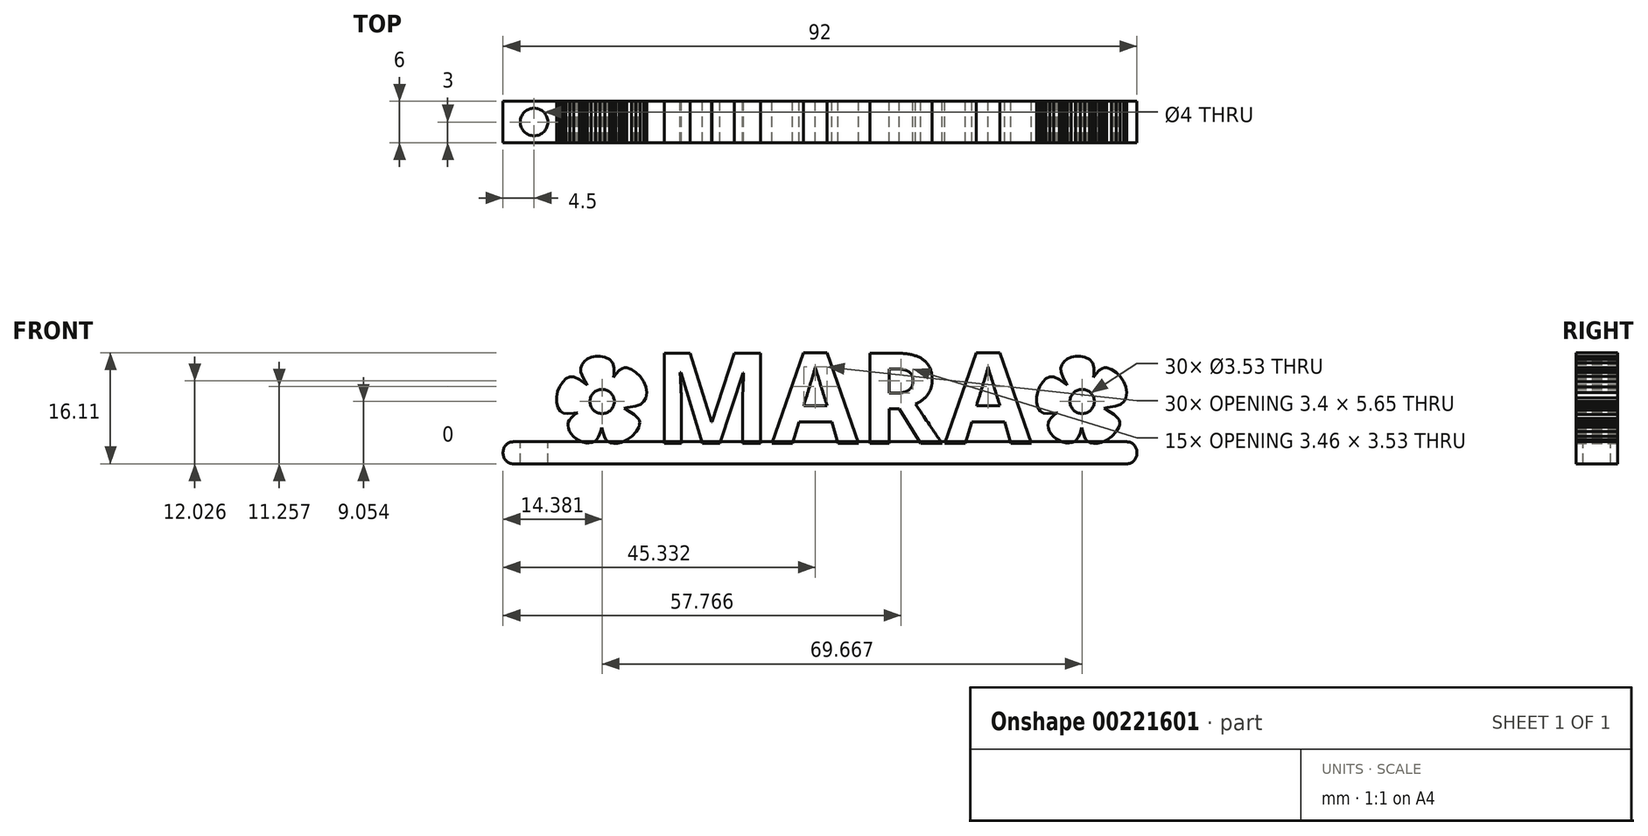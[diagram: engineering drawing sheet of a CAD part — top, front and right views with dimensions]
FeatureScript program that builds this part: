
annotation { "Feature Type Name" : "Feature", "Feature Type Description" : "" }
export const myFeature = defineFeature(function(context is Context, id is Id, definition is map)
    precondition{}
    {
        {
            var Q0;
            Q0=qCreatedBy(makeId("Front.planeOp"),FACE);
            var sketch = newSketch(context, id + "F0", { "sketchPlane" : qUnion([Q0])});
            skText(sketch, "E0", { "text": "   MARA", "fontName": "OpenSans-Bold.ttf"});
            skLineSegment(sketch, "E1.0.0", {"start": v(-9.3, 0.1) * mm, "end": v(-8.53, 0.46) * mm});
            skLineSegment(sketch, "E1.0.1", {"start": v(-8.53, 0.46) * mm, "end": v(-7.79, 1.02) * mm});
            skLineSegment(sketch, "E1.0.2", {"start": v(-7.79, 1.02) * mm, "end": v(-7.18, 1.67) * mm});
            skLineSegment(sketch, "E1.0.3", {"start": v(-7.18, 1.67) * mm, "end": v(-6.78, 2.35) * mm});
            skLineSegment(sketch, "E1.0.4", {"start": v(-6.78, 2.35) * mm, "end": v(-6.68, 2.7) * mm});
            skLineSegment(sketch, "E1.0.5", {"start": v(-6.68, 2.7) * mm, "end": v(-6.67, 3.02) * mm});
            skLineSegment(sketch, "E1.0.6", {"start": v(-6.67, 3.02) * mm, "end": v(-6.73, 3.33) * mm});
            skLineSegment(sketch, "E1.0.7", {"start": v(-6.73, 3.33) * mm, "end": v(-6.89, 3.62) * mm});
            skLineSegment(sketch, "E1.0.8", {"start": v(-6.89, 3.62) * mm, "end": v(-7.48, 4.2) * mm});
            skLineSegment(sketch, "E1.0.9", {"start": v(-7.48, 4.2) * mm, "end": v(-8.5, 4.79) * mm});
            skLineSegment(sketch, "E1.0.10", {"start": v(-8.5, 4.79) * mm, "end": v(-8.93, 5.06) * mm});
            skLineSegment(sketch, "E1.0.11", {"start": v(-8.93, 5.06) * mm, "end": v(-8.42, 5.16) * mm});
            skLineSegment(sketch, "E1.0.12", {"start": v(-8.42, 5.16) * mm, "end": v(-7.31, 5.37) * mm});
            skLineSegment(sketch, "E1.0.13", {"start": v(-7.31, 5.37) * mm, "end": v(-6.55, 5.65) * mm});
            skLineSegment(sketch, "E1.0.14", {"start": v(-6.55, 5.65) * mm, "end": v(-6.05, 6.04) * mm});
            skLineSegment(sketch, "E1.0.15", {"start": v(-6.05, 6.04) * mm, "end": v(-5.76, 6.58) * mm});
            skLineSegment(sketch, "E1.0.16", {"start": v(-5.76, 6.58) * mm, "end": v(-5.64, 7.33) * mm});
            skLineSegment(sketch, "E1.0.17", {"start": v(-5.64, 7.33) * mm, "end": v(-5.78, 8.14) * mm});
            skLineSegment(sketch, "E1.0.18", {"start": v(-5.78, 8.14) * mm, "end": v(-6.1, 8.93) * mm});
            skLineSegment(sketch, "E1.0.19", {"start": v(-6.1, 8.93) * mm, "end": v(-6.6, 9.67) * mm});
            skLineSegment(sketch, "E1.0.20", {"start": v(-6.6, 9.67) * mm, "end": v(-7.2, 10.28) * mm});
            skLineSegment(sketch, "E1.0.21", {"start": v(-7.2, 10.28) * mm, "end": v(-7.86, 10.72) * mm});
            skLineSegment(sketch, "E1.0.22", {"start": v(-7.86, 10.72) * mm, "end": v(-8.55, 10.93) * mm});
            skLineSegment(sketch, "E1.0.23", {"start": v(-8.55, 10.93) * mm, "end": v(-8.88, 10.93) * mm});
            skLineSegment(sketch, "E1.0.24", {"start": v(-8.88, 10.93) * mm, "end": v(-9.2, 10.85) * mm});
            skLineSegment(sketch, "E1.0.25", {"start": v(-9.2, 10.85) * mm, "end": v(-9.65, 10.56) * mm});
            skLineSegment(sketch, "E1.0.26", {"start": v(-9.65, 10.56) * mm, "end": v(-10.14, 9.98) * mm});
            skLineSegment(sketch, "E1.0.27", {"start": v(-10.14, 9.98) * mm, "end": v(-10.45, 9.58) * mm});
            skLineSegment(sketch, "E1.0.28", {"start": v(-10.45, 9.58) * mm, "end": v(-10.4, 10.03) * mm});
            skLineSegment(sketch, "E1.0.29", {"start": v(-10.4, 10.03) * mm, "end": v(-10.4, 10.93) * mm});
            skLineSegment(sketch, "E1.0.30", {"start": v(-10.4, 10.93) * mm, "end": v(-10.6, 11.63) * mm});
            skLineSegment(sketch, "E1.0.31", {"start": v(-10.6, 11.63) * mm, "end": v(-11.04, 12.15) * mm});
            skLineSegment(sketch, "E1.0.32", {"start": v(-11.04, 12.15) * mm, "end": v(-11.71, 12.5) * mm});
            skLineSegment(sketch, "E1.0.33", {"start": v(-11.71, 12.5) * mm, "end": v(-12.4, 12.64) * mm});
            skLineSegment(sketch, "E1.0.34", {"start": v(-12.4, 12.64) * mm, "end": v(-13.07, 12.62) * mm});
            skLineSegment(sketch, "E1.0.35", {"start": v(-13.07, 12.62) * mm, "end": v(-13.7, 12.47) * mm});
            skLineSegment(sketch, "E1.0.36", {"start": v(-13.7, 12.47) * mm, "end": v(-14.26, 12.2) * mm});
            skLineSegment(sketch, "E1.0.37", {"start": v(-14.26, 12.2) * mm, "end": v(-14.72, 11.83) * mm});
            skLineSegment(sketch, "E1.0.38", {"start": v(-14.72, 11.83) * mm, "end": v(-15.05, 11.38) * mm});
            skLineSegment(sketch, "E1.0.39", {"start": v(-15.05, 11.38) * mm, "end": v(-15.22, 10.87) * mm});
            skLineSegment(sketch, "E1.0.40", {"start": v(-15.22, 10.87) * mm, "end": v(-15.2, 10.3) * mm});
            skLineSegment(sketch, "E1.0.41", {"start": v(-15.2, 10.3) * mm, "end": v(-14.83, 9.4) * mm});
            skLineSegment(sketch, "E1.0.42", {"start": v(-14.83, 9.4) * mm, "end": v(-14.35, 8.55) * mm});
            skLineSegment(sketch, "E1.0.43", {"start": v(-14.35, 8.55) * mm, "end": v(-14.3, 8.4) * mm});
            skLineSegment(sketch, "E1.0.44", {"start": v(-14.3, 8.4) * mm, "end": v(-14.48, 8.53) * mm});
            skLineSegment(sketch, "E1.0.45", {"start": v(-14.48, 8.53) * mm, "end": v(-15.4, 9.23) * mm});
            skLineSegment(sketch, "E1.0.46", {"start": v(-15.4, 9.23) * mm, "end": v(-16.22, 9.63) * mm});
            skLineSegment(sketch, "E1.0.47", {"start": v(-16.22, 9.63) * mm, "end": v(-16.8, 9.63) * mm});
            skLineSegment(sketch, "E1.0.48", {"start": v(-16.8, 9.63) * mm, "end": v(-17.36, 9.37) * mm});
            skLineSegment(sketch, "E1.0.49", {"start": v(-17.36, 9.37) * mm, "end": v(-17.85, 8.9) * mm});
            skLineSegment(sketch, "E1.0.50", {"start": v(-17.85, 8.9) * mm, "end": v(-18.26, 8.26) * mm});
            skLineSegment(sketch, "E1.0.51", {"start": v(-18.26, 8.26) * mm, "end": v(-18.56, 7.51) * mm});
            skLineSegment(sketch, "E1.0.52", {"start": v(-18.56, 7.51) * mm, "end": v(-18.72, 6.71) * mm});
            skLineSegment(sketch, "E1.0.53", {"start": v(-18.72, 6.71) * mm, "end": v(-18.72, 5.9) * mm});
            skLineSegment(sketch, "E1.0.54", {"start": v(-18.72, 5.9) * mm, "end": v(-18.52, 5.16) * mm});
            skLineSegment(sketch, "E1.0.55", {"start": v(-18.52, 5.16) * mm, "end": v(-18.2, 4.64) * mm});
            skLineSegment(sketch, "E1.0.56", {"start": v(-18.2, 4.64) * mm, "end": v(-17.75, 4.36) * mm});
            skLineSegment(sketch, "E1.0.57", {"start": v(-17.75, 4.36) * mm, "end": v(-17.1, 4.27) * mm});
            skLineSegment(sketch, "E1.0.58", {"start": v(-17.1, 4.27) * mm, "end": v(-16.21, 4.37) * mm});
            skLineSegment(sketch, "E1.0.59", {"start": v(-16.21, 4.37) * mm, "end": v(-15.7, 4.43) * mm});
            skLineSegment(sketch, "E1.0.60", {"start": v(-15.7, 4.43) * mm, "end": v(-15.67, 4.4) * mm});
            skLineSegment(sketch, "E1.0.61", {"start": v(-15.67, 4.4) * mm, "end": v(-15.78, 4.33) * mm});
            skLineSegment(sketch, "E1.0.62", {"start": v(-15.78, 4.33) * mm, "end": v(-16.17, 4.07) * mm});
            skLineSegment(sketch, "E1.0.63", {"start": v(-16.17, 4.07) * mm, "end": v(-16.55, 3.71) * mm});
            skLineSegment(sketch, "E1.0.64", {"start": v(-16.55, 3.71) * mm, "end": v(-16.87, 3.33) * mm});
            skLineSegment(sketch, "E1.0.65", {"start": v(-16.87, 3.33) * mm, "end": v(-17.04, 3) * mm});
            skLineSegment(sketch, "E1.0.66", {"start": v(-17.04, 3) * mm, "end": v(-17.08, 2.6) * mm});
            skLineSegment(sketch, "E1.0.67", {"start": v(-17.08, 2.6) * mm, "end": v(-17.02, 2.2) * mm});
            skLineSegment(sketch, "E1.0.68", {"start": v(-17.02, 2.2) * mm, "end": v(-16.87, 1.78) * mm});
            skLineSegment(sketch, "E1.0.69", {"start": v(-16.87, 1.78) * mm, "end": v(-16.62, 1.39) * mm});
            skLineSegment(sketch, "E1.0.70", {"start": v(-16.62, 1.39) * mm, "end": v(-16.3, 1.02) * mm});
            skLineSegment(sketch, "E1.0.71", {"start": v(-16.3, 1.02) * mm, "end": v(-15.9, 0.69) * mm});
            skLineSegment(sketch, "E1.0.72", {"start": v(-15.9, 0.69) * mm, "end": v(-15.45, 0.4) * mm});
            skLineSegment(sketch, "E1.0.73", {"start": v(-15.45, 0.4) * mm, "end": v(-14.95, 0.2) * mm});
            skLineSegment(sketch, "E1.0.74", {"start": v(-14.95, 0.2) * mm, "end": v(-14.44, 0.06) * mm});
            skLineSegment(sketch, "E1.0.75", {"start": v(-14.44, 0.06) * mm, "end": v(-13.98, 0.02) * mm});
            skLineSegment(sketch, "E1.0.76", {"start": v(-13.98, 0.02) * mm, "end": v(-13.58, 0.08) * mm});
            skLineSegment(sketch, "E1.0.77", {"start": v(-13.58, 0.08) * mm, "end": v(-13.23, 0.23) * mm});
            skLineSegment(sketch, "E1.0.78", {"start": v(-13.23, 0.23) * mm, "end": v(-12.92, 0.49) * mm});
            skLineSegment(sketch, "E1.0.79", {"start": v(-12.92, 0.49) * mm, "end": v(-12.67, 0.84) * mm});
            skLineSegment(sketch, "E1.0.80", {"start": v(-12.67, 0.84) * mm, "end": v(-12.46, 1.28) * mm});
            skLineSegment(sketch, "E1.0.81", {"start": v(-12.46, 1.28) * mm, "end": v(-12.3, 1.83) * mm});
            skLineSegment(sketch, "E1.0.82", {"start": v(-12.3, 1.83) * mm, "end": v(-12.19, 2.26) * mm});
            skLineSegment(sketch, "E1.0.83", {"start": v(-12.19, 2.26) * mm, "end": v(-12.13, 2.1) * mm});
            skLineSegment(sketch, "E1.0.84", {"start": v(-12.13, 2.1) * mm, "end": v(-12.01, 1.53) * mm});
            skLineSegment(sketch, "E1.0.85", {"start": v(-12.01, 1.53) * mm, "end": v(-11.82, 1) * mm});
            skLineSegment(sketch, "E1.0.86", {"start": v(-11.82, 1) * mm, "end": v(-11.6, 0.55) * mm});
            skLineSegment(sketch, "E1.0.87", {"start": v(-11.6, 0.55) * mm, "end": v(-11.35, 0.26) * mm});
            skLineSegment(sketch, "E1.0.88", {"start": v(-11.35, 0.26) * mm, "end": v(-10.95, 0.05) * mm});
            skLineSegment(sketch, "E1.0.89", {"start": v(-10.95, 0.05) * mm, "end": v(-10.46, -0.04) * mm});
            skLineSegment(sketch, "E1.0.90", {"start": v(-10.46, -0.04) * mm, "end": v(-9.9, -0.03) * mm});
            skLineSegment(sketch, "E1.0.91", {"start": v(-9.9, -0.03) * mm, "end": v(-9.3, 0.1) * mm});
            skCircle(sketch, "E2", {"center": v(-12.12, 6.05) * mm, "radius": 1.77 * mm});
            skCircle(sketch, "E3.1.0.0", {"center": v(57.55, 6.05) * mm, "radius": 1.77 * mm});
            skLineSegment(sketch, "E3.1.0.1", {"start": v(59.22, 9.58) * mm, "end": v(59.26, 10.03) * mm});
            skLineSegment(sketch, "E3.1.0.2", {"start": v(62.47, 10.28) * mm, "end": v(61.8, 10.72) * mm});
            skLineSegment(sketch, "E3.1.0.3", {"start": v(50.95, 5.9) * mm, "end": v(51.15, 5.16) * mm});
            skLineSegment(sketch, "E3.1.0.4", {"start": v(55.4, 12.2) * mm, "end": v(54.94, 11.83) * mm});
            skLineSegment(sketch, "E3.1.0.5", {"start": v(53.37, 1.02) * mm, "end": v(53.76, 0.69) * mm});
            skLineSegment(sketch, "E3.1.0.6", {"start": v(53.45, 9.63) * mm, "end": v(52.86, 9.63) * mm});
            skLineSegment(sketch, "E3.1.0.7", {"start": v(51.1, 7.51) * mm, "end": v(50.95, 6.71) * mm});
            skLineSegment(sketch, "E3.1.0.8", {"start": v(54.27, 9.23) * mm, "end": v(53.45, 9.63) * mm});
            skLineSegment(sketch, "E3.1.0.9", {"start": v(52.86, 9.63) * mm, "end": v(52.31, 9.37) * mm});
            skLineSegment(sketch, "E3.1.0.10", {"start": v(59.53, 9.98) * mm, "end": v(59.22, 9.58) * mm});
            skLineSegment(sketch, "E3.1.0.11", {"start": v(59.07, 11.63) * mm, "end": v(58.63, 12.15) * mm});
            skLineSegment(sketch, "E3.1.0.12", {"start": v(58.63, 12.15) * mm, "end": v(57.95, 12.5) * mm});
            skLineSegment(sketch, "E3.1.0.13", {"start": v(59.28, 10.93) * mm, "end": v(59.07, 11.63) * mm});
            skLineSegment(sketch, "E3.1.0.14", {"start": v(54.21, 0.4) * mm, "end": v(54.72, 0.2) * mm});
            skLineSegment(sketch, "E3.1.0.15", {"start": v(59.77, -0.03) * mm, "end": v(60.36, 0.1) * mm});
            skLineSegment(sketch, "E3.1.0.16", {"start": v(50.95, 6.71) * mm, "end": v(50.95, 5.9) * mm});
            skLineSegment(sketch, "E3.1.0.17", {"start": v(60.36, 0.1) * mm, "end": v(61.14, 0.46) * mm});
            skLineSegment(sketch, "E3.1.0.18", {"start": v(53.76, 0.69) * mm, "end": v(54.21, 0.4) * mm});
            skLineSegment(sketch, "E3.1.0.19", {"start": v(51.15, 5.16) * mm, "end": v(51.47, 4.64) * mm});
            skLineSegment(sketch, "E3.1.0.20", {"start": v(62.35, 5.37) * mm, "end": v(63.12, 5.65) * mm});
            skLineSegment(sketch, "E3.1.0.21", {"start": v(61.14, 0.46) * mm, "end": v(61.88, 1.02) * mm});
            skLineSegment(sketch, "E3.1.0.22", {"start": v(63.07, 9.67) * mm, "end": v(62.47, 10.28) * mm});
            skLineSegment(sketch, "E3.1.0.23", {"start": v(59.26, 10.03) * mm, "end": v(59.28, 10.93) * mm});
            skLineSegment(sketch, "E3.1.0.24", {"start": v(52.31, 9.37) * mm, "end": v(51.81, 8.9) * mm});
            skLineSegment(sketch, "E3.1.0.25", {"start": v(57.95, 12.5) * mm, "end": v(57.27, 12.64) * mm});
            skLineSegment(sketch, "E3.1.0.26", {"start": v(56.6, 12.62) * mm, "end": v(55.96, 12.47) * mm});
            skLineSegment(sketch, "E3.1.0.27", {"start": v(62.5, 1.67) * mm, "end": v(62.88, 2.35) * mm});
            skLineSegment(sketch, "E3.1.0.28", {"start": v(63.56, 8.93) * mm, "end": v(63.07, 9.67) * mm});
            skLineSegment(sketch, "E3.1.0.29", {"start": v(57.27, 12.64) * mm, "end": v(56.6, 12.62) * mm});
            skLineSegment(sketch, "E3.1.0.30", {"start": v(61.88, 1.02) * mm, "end": v(62.5, 1.67) * mm});
            skLineSegment(sketch, "E3.1.0.31", {"start": v(51.81, 8.9) * mm, "end": v(51.4, 8.26) * mm});
            skLineSegment(sketch, "E3.1.0.32", {"start": v(51.4, 8.26) * mm, "end": v(51.1, 7.51) * mm});
            skLineSegment(sketch, "E3.1.0.33", {"start": v(55.96, 12.47) * mm, "end": v(55.4, 12.2) * mm});
            skLineSegment(sketch, "E3.1.0.34", {"start": v(62.88, 2.35) * mm, "end": v(62.98, 2.7) * mm});
            skLineSegment(sketch, "E3.1.0.35", {"start": v(52.86, 9.63) * mm, "end": v(52.31, 9.37) * mm});
            skLineSegment(sketch, "E3.1.0.36", {"start": v(57.27, 12.64) * mm, "end": v(56.6, 12.62) * mm});
            skLineSegment(sketch, "E3.1.0.37", {"start": v(62.35, 5.37) * mm, "end": v(63.12, 5.65) * mm});
            skLineSegment(sketch, "E3.1.0.38", {"start": v(58.71, 0.05) * mm, "end": v(59.21, -0.04) * mm});
            skLineSegment(sketch, "E3.1.0.39", {"start": v(63.56, 8.93) * mm, "end": v(63.07, 9.67) * mm});
            skLineSegment(sketch, "E3.1.0.40", {"start": v(59.77, -0.03) * mm, "end": v(60.36, 0.1) * mm});
            skLineSegment(sketch, "E3.1.0.41", {"start": v(59.53, 9.98) * mm, "end": v(59.22, 9.58) * mm});
            skLineSegment(sketch, "E3.1.0.42", {"start": v(61.88, 1.02) * mm, "end": v(62.5, 1.67) * mm});
            skLineSegment(sketch, "E3.1.0.43", {"start": v(62.88, 2.35) * mm, "end": v(62.98, 2.7) * mm});
            skLineSegment(sketch, "E3.1.0.44", {"start": v(50.95, 6.71) * mm, "end": v(50.95, 5.9) * mm});
            skLineSegment(sketch, "E3.1.0.45", {"start": v(60.36, 0.1) * mm, "end": v(61.14, 0.46) * mm});
            skLineSegment(sketch, "E3.1.0.46", {"start": v(56.6, 12.62) * mm, "end": v(55.96, 12.47) * mm});
            skLineSegment(sketch, "E3.1.0.47", {"start": v(55.4, 12.2) * mm, "end": v(54.94, 11.83) * mm});
            skLineSegment(sketch, "E3.1.0.48", {"start": v(54.21, 0.4) * mm, "end": v(54.72, 0.2) * mm});
            skLineSegment(sketch, "E3.1.0.49", {"start": v(59.26, 10.03) * mm, "end": v(59.28, 10.93) * mm});
            skLineSegment(sketch, "E3.1.0.50", {"start": v(59.22, 9.58) * mm, "end": v(59.26, 10.03) * mm});
            skLineSegment(sketch, "E3.1.0.51", {"start": v(59.21, -0.04) * mm, "end": v(59.77, -0.03) * mm});
            skLineSegment(sketch, "E3.1.0.52", {"start": v(53.45, 9.63) * mm, "end": v(52.86, 9.63) * mm});
            skLineSegment(sketch, "E3.1.0.53", {"start": v(59.28, 10.93) * mm, "end": v(59.07, 11.63) * mm});
            skLineSegment(sketch, "E3.1.0.54", {"start": v(62.47, 10.28) * mm, "end": v(61.8, 10.72) * mm});
            skLineSegment(sketch, "E3.1.0.55", {"start": v(51.81, 8.9) * mm, "end": v(51.4, 8.26) * mm});
            skLineSegment(sketch, "E3.1.0.56", {"start": v(53.76, 0.69) * mm, "end": v(54.21, 0.4) * mm});
            skLineSegment(sketch, "E3.1.0.57", {"start": v(57.95, 12.5) * mm, "end": v(57.27, 12.64) * mm});
            skLineSegment(sketch, "E3.1.0.58", {"start": v(52.31, 9.37) * mm, "end": v(51.81, 8.9) * mm});
            skLineSegment(sketch, "E3.1.0.59", {"start": v(50.95, 5.9) * mm, "end": v(51.15, 5.16) * mm});
            skLineSegment(sketch, "E3.1.0.60", {"start": v(58.63, 12.15) * mm, "end": v(57.95, 12.5) * mm});
            skLineSegment(sketch, "E3.1.0.61", {"start": v(54.27, 9.23) * mm, "end": v(53.45, 9.63) * mm});
            skLineSegment(sketch, "E3.1.0.62", {"start": v(61.14, 0.46) * mm, "end": v(61.88, 1.02) * mm});
            skLineSegment(sketch, "E3.1.0.63", {"start": v(59.07, 11.63) * mm, "end": v(58.63, 12.15) * mm});
            skLineSegment(sketch, "E3.1.0.64", {"start": v(51.4, 8.26) * mm, "end": v(51.1, 7.51) * mm});
            skLineSegment(sketch, "E3.1.0.65", {"start": v(62.5, 1.67) * mm, "end": v(62.88, 2.35) * mm});
            skLineSegment(sketch, "E3.1.0.66", {"start": v(51.1, 7.51) * mm, "end": v(50.95, 6.71) * mm});
            skLineSegment(sketch, "E3.1.0.67", {"start": v(53.37, 1.02) * mm, "end": v(53.76, 0.69) * mm});
            skLineSegment(sketch, "E3.1.0.68", {"start": v(51.15, 5.16) * mm, "end": v(51.47, 4.64) * mm});
            skLineSegment(sketch, "E3.1.0.69", {"start": v(55.96, 12.47) * mm, "end": v(55.4, 12.2) * mm});
            skLineSegment(sketch, "E3.1.0.70", {"start": v(63.07, 9.67) * mm, "end": v(62.47, 10.28) * mm});
            skLineSegment(sketch, "E3.1.0.71", {"start": v(54.94, 11.83) * mm, "end": v(54.61, 11.38) * mm});
            skLineSegment(sketch, "E3.1.0.72", {"start": v(61.8, 10.72) * mm, "end": v(61.12, 10.93) * mm});
            skLineSegment(sketch, "E3.1.0.73", {"start": v(63.61, 6.04) * mm, "end": v(63.91, 6.58) * mm});
            skLineSegment(sketch, "E3.1.0.74", {"start": v(62.98, 2.7) * mm, "end": v(63, 3.02) * mm});
            skLineSegment(sketch, "E3.1.0.75", {"start": v(61.12, 10.93) * mm, "end": v(60.79, 10.93) * mm});
            skLineSegment(sketch, "E3.1.0.76", {"start": v(51.47, 4.64) * mm, "end": v(51.92, 4.36) * mm});
            skLineSegment(sketch, "E3.1.0.77", {"start": v(60.46, 10.85) * mm, "end": v(60.02, 10.56) * mm});
            skLineSegment(sketch, "E3.1.0.78", {"start": v(61.25, 5.16) * mm, "end": v(62.35, 5.37) * mm});
            skLineSegment(sketch, "E3.1.0.79", {"start": v(63, 3.02) * mm, "end": v(62.94, 3.33) * mm});
            skLineSegment(sketch, "E3.1.0.80", {"start": v(62.94, 3.33) * mm, "end": v(62.78, 3.62) * mm});
            skLineSegment(sketch, "E3.1.0.81", {"start": v(62.18, 4.2) * mm, "end": v(61.17, 4.79) * mm});
            skLineSegment(sketch, "E3.1.0.82", {"start": v(64.02, 7.33) * mm, "end": v(63.9, 8.14) * mm});
            skLineSegment(sketch, "E3.1.0.83", {"start": v(53.04, 1.39) * mm, "end": v(53.37, 1.02) * mm});
            skLineSegment(sketch, "E3.1.0.84", {"start": v(55.23, 0.06) * mm, "end": v(55.68, 0.02) * mm});
            skLineSegment(sketch, "E3.1.0.85", {"start": v(60.74, 5.06) * mm, "end": v(61.25, 5.16) * mm});
            skLineSegment(sketch, "E3.1.0.86", {"start": v(58.31, 0.26) * mm, "end": v(58.71, 0.05) * mm});
            skLineSegment(sketch, "E3.1.0.87", {"start": v(54.61, 11.38) * mm, "end": v(54.45, 10.87) * mm});
            skLineSegment(sketch, "E3.1.0.88", {"start": v(63.91, 6.58) * mm, "end": v(64.02, 7.33) * mm});
            skLineSegment(sketch, "E3.1.0.89", {"start": v(58.71, 0.05) * mm, "end": v(59.21, -0.04) * mm});
            skLineSegment(sketch, "E3.1.0.90", {"start": v(61.17, 4.79) * mm, "end": v(60.74, 5.06) * mm});
            skLineSegment(sketch, "E3.1.0.91", {"start": v(54.72, 0.2) * mm, "end": v(55.23, 0.06) * mm});
            skLineSegment(sketch, "E3.1.0.92", {"start": v(54.47, 10.3) * mm, "end": v(54.84, 9.4) * mm});
            skLineSegment(sketch, "E3.1.0.93", {"start": v(52.8, 1.78) * mm, "end": v(53.04, 1.39) * mm});
            skLineSegment(sketch, "E3.1.0.94", {"start": v(62.78, 3.62) * mm, "end": v(62.18, 4.2) * mm});
            skLineSegment(sketch, "E3.1.0.95", {"start": v(59.21, -0.04) * mm, "end": v(59.77, -0.03) * mm});
            skLineSegment(sketch, "E3.1.0.96", {"start": v(54.45, 10.87) * mm, "end": v(54.47, 10.3) * mm});
            skLineSegment(sketch, "E3.1.0.97", {"start": v(63.12, 5.65) * mm, "end": v(63.61, 6.04) * mm});
            skLineSegment(sketch, "E3.1.0.98", {"start": v(60.79, 10.93) * mm, "end": v(60.46, 10.85) * mm});
            skLineSegment(sketch, "E3.1.0.99", {"start": v(60.02, 10.56) * mm, "end": v(59.53, 9.98) * mm});
            skLineSegment(sketch, "E3.1.0.100", {"start": v(55.68, 0.02) * mm, "end": v(56.09, 0.08) * mm});
            skLineSegment(sketch, "E3.1.0.101", {"start": v(52.64, 2.2) * mm, "end": v(52.8, 1.78) * mm});
            skLineSegment(sketch, "E3.1.0.102", {"start": v(63.9, 8.14) * mm, "end": v(63.56, 8.93) * mm});
            skLineSegment(sketch, "E3.1.0.103", {"start": v(61.17, 4.79) * mm, "end": v(60.74, 5.06) * mm});
            skLineSegment(sketch, "E3.1.0.104", {"start": v(60.74, 5.06) * mm, "end": v(61.25, 5.16) * mm});
            skLineSegment(sketch, "E3.1.0.105", {"start": v(51.47, 4.64) * mm, "end": v(51.92, 4.36) * mm});
            skLineSegment(sketch, "E3.1.0.106", {"start": v(58.07, 0.55) * mm, "end": v(58.31, 0.26) * mm});
            skLineSegment(sketch, "E3.1.0.107", {"start": v(58.31, 0.26) * mm, "end": v(58.71, 0.05) * mm});
            skLineSegment(sketch, "E3.1.0.108", {"start": v(52.8, 1.78) * mm, "end": v(53.04, 1.39) * mm});
            skLineSegment(sketch, "E3.1.0.109", {"start": v(62.78, 3.62) * mm, "end": v(62.18, 4.2) * mm});
            skLineSegment(sketch, "E3.1.0.110", {"start": v(61.25, 5.16) * mm, "end": v(62.35, 5.37) * mm});
            skLineSegment(sketch, "E3.1.0.111", {"start": v(54.47, 10.3) * mm, "end": v(54.84, 9.4) * mm});
            skLineSegment(sketch, "E3.1.0.112", {"start": v(63.12, 5.65) * mm, "end": v(63.61, 6.04) * mm});
            skLineSegment(sketch, "E3.1.0.113", {"start": v(60.02, 10.56) * mm, "end": v(59.53, 9.98) * mm});
            skLineSegment(sketch, "E3.1.0.114", {"start": v(63.91, 6.58) * mm, "end": v(64.02, 7.33) * mm});
            skLineSegment(sketch, "E3.1.0.115", {"start": v(54.45, 10.87) * mm, "end": v(54.47, 10.3) * mm});
            skLineSegment(sketch, "E3.1.0.116", {"start": v(60.79, 10.93) * mm, "end": v(60.46, 10.85) * mm});
            skLineSegment(sketch, "E3.1.0.117", {"start": v(55.68, 0.02) * mm, "end": v(56.09, 0.08) * mm});
            skLineSegment(sketch, "E3.1.0.118", {"start": v(60.46, 10.85) * mm, "end": v(60.02, 10.56) * mm});
            skLineSegment(sketch, "E3.1.0.119", {"start": v(55.23, 0.06) * mm, "end": v(55.68, 0.02) * mm});
            skLineSegment(sketch, "E3.1.0.120", {"start": v(54.72, 0.2) * mm, "end": v(55.23, 0.06) * mm});
            skLineSegment(sketch, "E3.1.0.121", {"start": v(62.18, 4.2) * mm, "end": v(61.17, 4.79) * mm});
            skLineSegment(sketch, "E3.1.0.122", {"start": v(63.61, 6.04) * mm, "end": v(63.91, 6.58) * mm});
            skLineSegment(sketch, "E3.1.0.123", {"start": v(52.58, 2.6) * mm, "end": v(52.64, 2.2) * mm});
            skLineSegment(sketch, "E3.1.0.124", {"start": v(62.98, 2.7) * mm, "end": v(63, 3.02) * mm});
            skLineSegment(sketch, "E3.1.0.125", {"start": v(53.04, 1.39) * mm, "end": v(53.37, 1.02) * mm});
            skLineSegment(sketch, "E3.1.0.126", {"start": v(63.9, 8.14) * mm, "end": v(63.56, 8.93) * mm});
            skLineSegment(sketch, "E3.1.0.127", {"start": v(64.02, 7.33) * mm, "end": v(63.9, 8.14) * mm});
            skLineSegment(sketch, "E3.1.0.128", {"start": v(63, 3.02) * mm, "end": v(62.94, 3.33) * mm});
            skLineSegment(sketch, "E3.1.0.129", {"start": v(52.64, 2.2) * mm, "end": v(52.8, 1.78) * mm});
            skLineSegment(sketch, "E3.1.0.130", {"start": v(62.94, 3.33) * mm, "end": v(62.78, 3.62) * mm});
            skLineSegment(sketch, "E3.1.0.131", {"start": v(54.61, 11.38) * mm, "end": v(54.45, 10.87) * mm});
            skLineSegment(sketch, "E3.1.0.132", {"start": v(61.12, 10.93) * mm, "end": v(60.79, 10.93) * mm});
            skLineSegment(sketch, "E3.1.0.133", {"start": v(61.8, 10.72) * mm, "end": v(61.12, 10.93) * mm});
            skLineSegment(sketch, "E3.1.0.134", {"start": v(54.94, 11.83) * mm, "end": v(54.61, 11.38) * mm});
            skLineSegment(sketch, "E3.1.0.135", {"start": v(52.58, 2.6) * mm, "end": v(52.64, 2.2) * mm});
            skLineSegment(sketch, "E3.1.0.136", {"start": v(53.45, 4.37) * mm, "end": v(53.96, 4.43) * mm});
            skLineSegment(sketch, "E3.1.0.137", {"start": v(57.66, 1.53) * mm, "end": v(57.84, 1) * mm});
            skLineSegment(sketch, "E3.1.0.138", {"start": v(53.89, 4.33) * mm, "end": v(53.5, 4.07) * mm});
            skLineSegment(sketch, "E3.1.0.139", {"start": v(56.44, 0.23) * mm, "end": v(56.74, 0.49) * mm});
            skLineSegment(sketch, "E3.1.0.140", {"start": v(57, 0.84) * mm, "end": v(57.2, 1.28) * mm});
            skLineSegment(sketch, "E3.1.0.141", {"start": v(57.84, 1) * mm, "end": v(58.07, 0.55) * mm});
            skLineSegment(sketch, "E3.1.0.142", {"start": v(53.5, 4.07) * mm, "end": v(53.11, 3.71) * mm});
            skLineSegment(sketch, "E3.1.0.143", {"start": v(57.54, 2.1) * mm, "end": v(57.66, 1.53) * mm});
            skLineSegment(sketch, "E3.1.0.144", {"start": v(56.74, 0.49) * mm, "end": v(57, 0.84) * mm});
            skLineSegment(sketch, "E3.1.0.145", {"start": v(52.56, 4.27) * mm, "end": v(53.45, 4.37) * mm});
            skLineSegment(sketch, "E3.1.0.146", {"start": v(53.11, 3.71) * mm, "end": v(52.8, 3.33) * mm});
            skLineSegment(sketch, "E3.1.0.147", {"start": v(51.92, 4.36) * mm, "end": v(52.56, 4.27) * mm});
            skLineSegment(sketch, "E3.1.0.148", {"start": v(57.2, 1.28) * mm, "end": v(57.36, 1.83) * mm});
            skLineSegment(sketch, "E3.1.0.149", {"start": v(57.48, 2.26) * mm, "end": v(57.54, 2.1) * mm});
            skLineSegment(sketch, "E3.1.0.150", {"start": v(52.8, 3.33) * mm, "end": v(52.63, 3) * mm});
            skLineSegment(sketch, "E3.1.0.151", {"start": v(58.07, 0.55) * mm, "end": v(58.31, 0.26) * mm});
            skLineSegment(sketch, "E3.1.0.152", {"start": v(57.36, 1.83) * mm, "end": v(57.48, 2.26) * mm});
            skLineSegment(sketch, "E3.1.0.153", {"start": v(52.63, 3) * mm, "end": v(52.58, 2.6) * mm});
            skLineSegment(sketch, "E3.1.0.154", {"start": v(56.09, 0.08) * mm, "end": v(56.44, 0.23) * mm});
            skLineSegment(sketch, "E3.1.0.155", {"start": v(54, 4.4) * mm, "end": v(53.89, 4.33) * mm});
            skLineSegment(sketch, "E3.1.0.156", {"start": v(57.48, 2.26) * mm, "end": v(57.54, 2.1) * mm});
            skLineSegment(sketch, "E3.1.0.157", {"start": v(52.56, 4.27) * mm, "end": v(53.45, 4.37) * mm});
            skLineSegment(sketch, "E3.1.0.158", {"start": v(57.66, 1.53) * mm, "end": v(57.84, 1) * mm});
            skLineSegment(sketch, "E3.1.0.159", {"start": v(53.96, 4.43) * mm, "end": v(54, 4.4) * mm});
            skLineSegment(sketch, "E3.1.0.160", {"start": v(53.11, 3.71) * mm, "end": v(52.8, 3.33) * mm});
            skLineSegment(sketch, "E3.1.0.161", {"start": v(51.92, 4.36) * mm, "end": v(52.56, 4.27) * mm});
            skLineSegment(sketch, "E3.1.0.162", {"start": v(53.45, 4.37) * mm, "end": v(53.96, 4.43) * mm});
            skLineSegment(sketch, "E3.1.0.163", {"start": v(56.09, 0.08) * mm, "end": v(56.44, 0.23) * mm});
            skLineSegment(sketch, "E3.1.0.164", {"start": v(53.5, 4.07) * mm, "end": v(53.11, 3.71) * mm});
            skLineSegment(sketch, "E3.1.0.165", {"start": v(57.54, 2.1) * mm, "end": v(57.66, 1.53) * mm});
            skLineSegment(sketch, "E3.1.0.166", {"start": v(57.36, 1.83) * mm, "end": v(57.48, 2.26) * mm});
            skLineSegment(sketch, "E3.1.0.167", {"start": v(53.89, 4.33) * mm, "end": v(53.5, 4.07) * mm});
            skLineSegment(sketch, "E3.1.0.168", {"start": v(56.44, 0.23) * mm, "end": v(56.74, 0.49) * mm});
            skLineSegment(sketch, "E3.1.0.169", {"start": v(52.63, 3) * mm, "end": v(52.58, 2.6) * mm});
            skLineSegment(sketch, "E3.1.0.170", {"start": v(57.84, 1) * mm, "end": v(58.07, 0.55) * mm});
            skLineSegment(sketch, "E3.1.0.171", {"start": v(56.74, 0.49) * mm, "end": v(57, 0.84) * mm});
            skLineSegment(sketch, "E3.1.0.172", {"start": v(57, 0.84) * mm, "end": v(57.2, 1.28) * mm});
            skLineSegment(sketch, "E3.1.0.173", {"start": v(52.8, 3.33) * mm, "end": v(52.63, 3) * mm});
            skLineSegment(sketch, "E3.1.0.174", {"start": v(57.2, 1.28) * mm, "end": v(57.36, 1.83) * mm});
            skLineSegment(sketch, "E3.1.0.175", {"start": v(54, 4.4) * mm, "end": v(53.89, 4.33) * mm});
            skLineSegment(sketch, "E3.1.0.176", {"start": v(53.96, 4.43) * mm, "end": v(54, 4.4) * mm});
            skLineSegment(sketch, "E3.1.0.177", {"start": v(55.38, 8.4) * mm, "end": v(55.19, 8.53) * mm});
            skLineSegment(sketch, "E3.1.0.178", {"start": v(55.31, 8.55) * mm, "end": v(55.38, 8.4) * mm});
            skLineSegment(sketch, "E3.1.0.179", {"start": v(54.84, 9.4) * mm, "end": v(55.31, 8.55) * mm});
            skLineSegment(sketch, "E3.1.0.180", {"start": v(55.19, 8.53) * mm, "end": v(54.27, 9.23) * mm});
            skLineSegment(sketch, "E3.1.0.181", {"start": v(55.31, 8.55) * mm, "end": v(55.38, 8.4) * mm});
            skLineSegment(sketch, "E3.1.0.182", {"start": v(54.84, 9.4) * mm, "end": v(55.31, 8.55) * mm});
            skLineSegment(sketch, "E3.1.0.183", {"start": v(55.19, 8.53) * mm, "end": v(54.27, 9.23) * mm});
            skLineSegment(sketch, "E3.1.0.184", {"start": v(55.38, 8.4) * mm, "end": v(55.19, 8.53) * mm});
            skLineSegment(sketch, "E3.direction1", {"start": v(-16.3, 1.02) * mm, "end": v(42.4, 1.02) * mm, "construction": true});
            const initialGuessF0  = {"E0": [-0.019, 0, 1, 0, 0.01317]};
            skSetInitialGuess(sketch, initialGuessF0);
            skSolve(sketch);
        }
        {
            var Q0;
            Q0=qSketchRegion(id+"F0",true);
            extrude(context, id + "F1", {"entities" : qUnion([Q0]), "endBound" : BoundingType.SYMMETRIC, "depth" : 6 * mm});
        }
        {
            var Q0;
            Q0=qCreatedBy(makeId("Top.planeOp"),FACE);
            var sketch = newSketch(context, id + "F2", { "sketchPlane" : qUnion([Q0])});
            skLineSegment(sketch, "E4.bottom", {"start": v(-19, 3) * mm, "end": v(65.5, 3) * mm});
            skLineSegment(sketch, "E4.top", {"start": v(-19, -3) * mm, "end": v(65.5, -3) * mm});
            skLineSegment(sketch, "E4.left", {"start": v(-19, 3) * mm, "end": v(-19, -3) * mm});
            skLineSegment(sketch, "E4.right", {"start": v(65.5, 3) * mm, "end": v(65.5, -3) * mm});
            skSolve(sketch);
        }
        {
            var Q0;
            Q0=makeQuery(id+"F2.imprint","IMPRINT",FACE,{"disambiguationData":[TD([[makeQuery(id+"F2.imprint","IMPRINT",EDGE,{"derivedFrom":sQuery(id+"F2.wireOp",EDGE,"E4.bottom")}),-1.0]])]});
            extrude(context, id + "F3", {"entities" : qUnion([Q0]), "depth" : 0.2 * mm});
        }
        {
            var Q0;
            Q0=makeQuery(id+"F3.opExtrude","CAP_FACE",FACE,{"disambiguationData":[OSD([sQuery(id+"F2.wireOp",EDGE,"E4.bottom"),sQuery(id+"F2.wireOp",EDGE,"E4.top"),sQuery(id+"F2.wireOp",EDGE,"E4.left"),sQuery(id+"F2.wireOp",EDGE,"E4.right")])],"isStart":true});
            extrude(context, id + "F4", {"entities" : qUnion([Q0]), "depth" : 3 * mm});
        }
        {
            var Q0;
            {var subQ0=sQuery(id+"F2.wireOp",EDGE,"E4.left");Q0=makeQuery(id+"FaVoHrOpcFZXiYX_6.opBoolean","MERGE",FACE,{"derivedFrom":[makeQuery(id+"F3.opExtrude","SWEPT_FACE",FACE,{"disambiguationData":[OSD([subQ0])]}),makeQuery(id+"F4.opExtrude","SWEPT_FACE",FACE,{"disambiguationData":[OSD([subQ0])]})]});}
            var sketch = newSketch(context, id + "F5", { "sketchPlane" : qUnion([Q0])});
            skLineSegment(sketch, "E5.bottom", {"start": v(-3, -3) * mm, "end": v(3, -3) * mm});
            skLineSegment(sketch, "E5.top", {"start": v(-3, 0.2) * mm, "end": v(3, 0.2) * mm});
            skLineSegment(sketch, "E5.left", {"start": v(-3, -3) * mm, "end": v(-3, 0.2) * mm});
            skLineSegment(sketch, "E5.right", {"start": v(3, -3) * mm, "end": v(3, 0.2) * mm});
            skSolve(sketch);
        }
        {
            var Q0;
            Q0=qSketchRegion(id+"F5",true);
            extrude(context, id + "F6", {"entities" : qUnion([Q0]), "operationType" : NewBodyOperationType.ADD, "depth" : 7.5 * mm});
        }
        {
            var Q0;
            Q0=makeQuery(id+"F6.opExtrude","CAP_EDGE",EDGE,{"disambiguationData":[OSD([sQuery(id+"F5.wireOp",EDGE,"E5.bottom")])],"isStart":false});
            var Q1;
            Q1=makeQuery(id+"F6.opExtrude","CAP_EDGE",EDGE,{"disambiguationData":[OSD([sQuery(id+"F5.wireOp",EDGE,"E5.top")])],"isStart":false});
            var Q2;
            Q2=makeQuery(id+"F4.opExtrude","CAP_EDGE",EDGE,{"disambiguationData":[OSD([sQuery(id+"F2.wireOp",EDGE,"E4.right")])],"isStart":false});
            fillet(context, id + "F7", {"entities" : qUnion([Q0, Q1, Q2]), "radius" : 1.5 * mm, "tangentPropagation" : true, "allowEdgeOverflow" : false});
        }
        {
            var Q0;
            {var subQ19=sQuery(id+"F2.wireOp",EDGE,"E4.top");var subQ20=sQuery(id+"F2.wireOp",EDGE,"E4.bottom");var subQ63=sQuery(id+"F0.wireOp",EDGE,"E0.sketch_text.stroke-2");var subQ66=sQuery(id+"F2.wireOp",EDGE,"E4.left");Q0=makeQuery(id+"F6.boolean.opBoolean","MERGE",FACE,{"derivedFrom":[makeQuery(id+"FaVoHrOpcFZXiYX_6.opBoolean","SPLIT",FACE,{"disambiguationData":[TD([makeQuery(id+"F1.opExtrude","SWEPT_FACE",FACE,{"disambiguationData":[OSD([subQ63])]})])],"derivedFrom":makeQuery(id+"F3.opExtrude","CAP_FACE",FACE,{"disambiguationData":[OSD([subQ20,subQ19,subQ66,sQuery(id+"F2.wireOp",EDGE,"E4.right")])],"isStart":false})}),makeQuery(id+"F6.opExtrude","SWEPT_FACE",FACE,{"disambiguationData":[OSD([sQuery(id+"F5.wireOp",EDGE,"E5.top")])]})]});}
            var sketch = newSketch(context, id + "F8", { "sketchPlane" : qUnion([Q0])});
            skCircle(sketch, "E6", {"center": v(-22, 0) * mm, "radius": 2 * mm});
            skSolve(sketch);
        }
        {
            var Q0;
            Q0=makeQuery(id+"F8.imprint","IMPRINT",FACE,{"disambiguationData":[TD([[makeQuery(id+"F8.imprint","IMPRINT",EDGE,{"derivedFrom":sQuery(id+"F8.wireOp",EDGE,"E6")}),1.0]])]});
            extrude(context, id + "F9", {"entities" : qUnion([Q0]), "operationType" : NewBodyOperationType.REMOVE, "oppositeDirection" : true, "depth" : 4 * mm});
        }
        {
            var Q0;
            Q0=makeQuery(id+"F3.opExtrude","CAP_EDGE",EDGE,{"disambiguationData":[OSD([sQuery(id+"F2.wireOp",EDGE,"E4.right")])],"isStart":false});
            fillet(context, id + "F10", {"entities" : qUnion([Q0]), "radius" : 1.5 * mm, "tangentPropagation" : true, "allowEdgeOverflow" : false});
        }
    });
